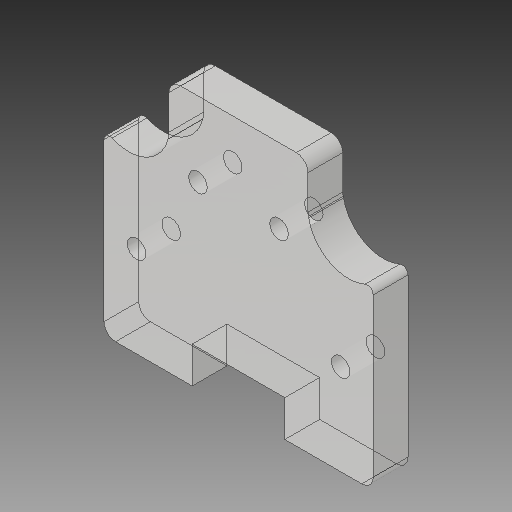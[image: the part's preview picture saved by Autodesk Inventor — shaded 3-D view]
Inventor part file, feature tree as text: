
AUTODESK INVENTOR PART (.ipt)
format: ipt  version: 2017 (Build 210142000, 142)  size: 161,792 bytes
history: native  units: mm
features: sketch x4, other x3, plane x1
ambient origin geometry x8: Origin, YZ Plane, XZ Plane, XY Plane, X Axis, Y Axis, Z Axis, Center Point
bodies: Solid1 (feature_tree)
feature tree (8):
  other  "Hotend Slide Part3.ipt"
  other  "Solid1::Hotend Slide Part3.ipt"
  other  "TaggingFeature1"
  sketch  "Sketch1"  dims[d0=10.0mm]
  sketch  "Sketch2"
  sketch  "Sketch3"
  sketch  "Sketch4"
  plane  "Work Plane1"
